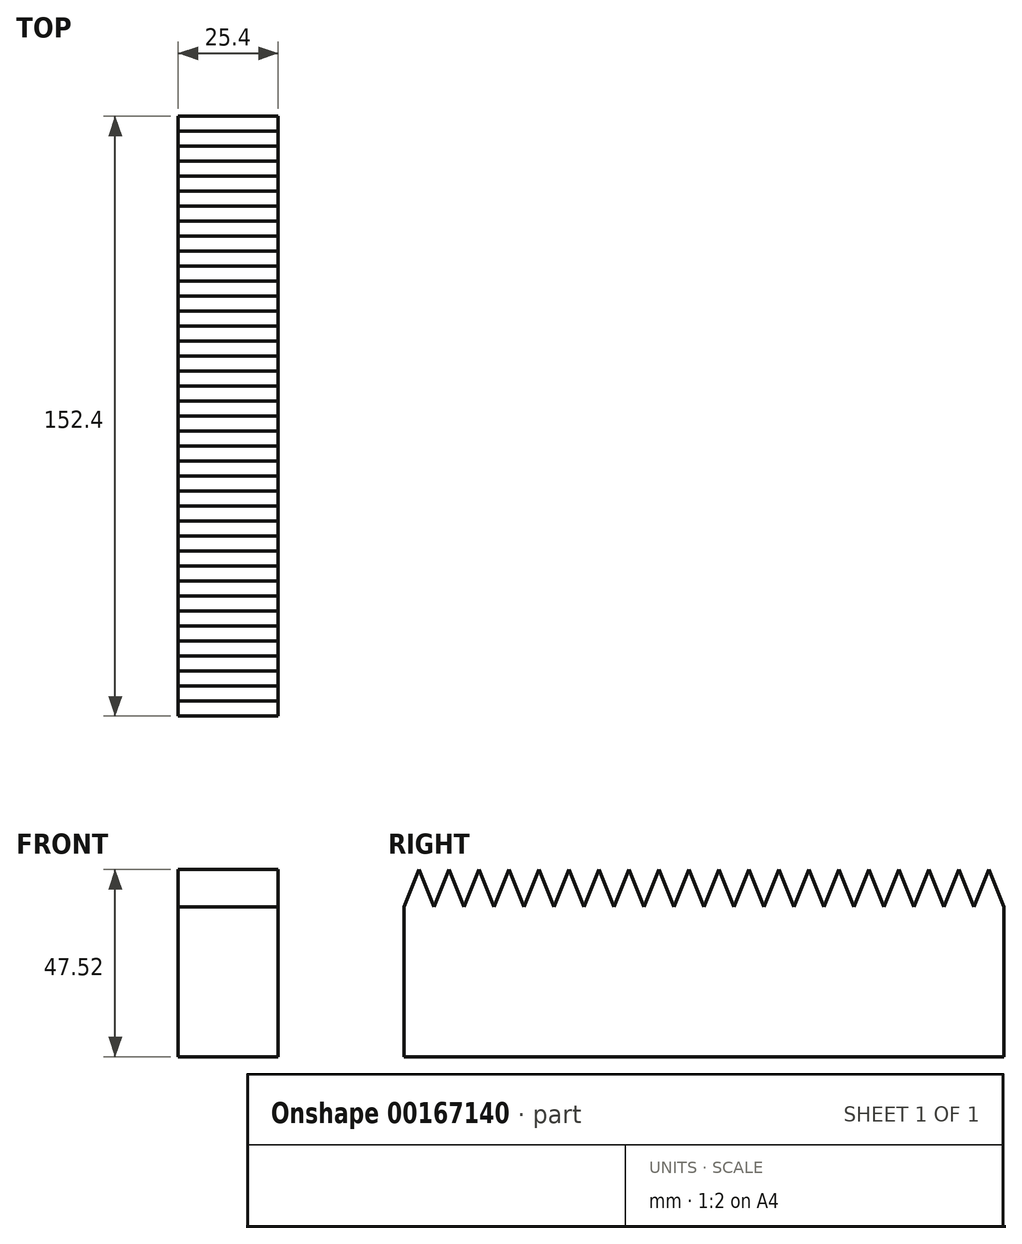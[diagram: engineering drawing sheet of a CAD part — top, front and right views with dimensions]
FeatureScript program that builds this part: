
annotation { "Feature Type Name" : "Feature", "Feature Type Description" : "" }
export const myFeature = defineFeature(function(context is Context, id is Id, definition is map)
    precondition{}
    {
        {
            var Q0;
            Q0=qCreatedBy(makeId("Right.planeOp"),FACE);
            var sketch = newSketch(context, id + "F0", { "sketchPlane" : qUnion([Q0])});
            skLineSegment(sketch, "E0.bottom", {"start": v(76.2, 19.05) * mm, "end": v(-76.2, 19.05) * mm});
            skLineSegment(sketch, "E0.top", {"start": v(76.2, -19.05) * mm, "end": v(-76.2, -19.05) * mm});
            skLineSegment(sketch, "E0.left", {"start": v(76.2, 19.05) * mm, "end": v(76.2, -19.05) * mm});
            skLineSegment(sketch, "E0.right", {"start": v(-76.2, 19.05) * mm, "end": v(-76.2, -19.05) * mm});
            skPoint(sketch, "E0.middle", {"position": v(0, 0) * mm});
            skLineSegment(sketch, "E1", {"start": v(-76.2, 19.05) * mm, "end": v(-72.39, 28.47) * mm});
            skLineSegment(sketch, "E2", {"start": v(-72.39, 28.47) * mm, "end": v(-68.58, 19.05) * mm});
            skLineSegment(sketch, "E3", {"start": v(-68.58, 19.05) * mm, "end": v(-76.2, 19.05) * mm});
            skLineSegment(sketch, "E4.1.0.0", {"start": v(-60.96, 19.05) * mm, "end": v(-68.58, 19.05) * mm});
            skLineSegment(sketch, "E4.1.0.1", {"start": v(-64.77, 28.47) * mm, "end": v(-60.96, 19.05) * mm});
            skLineSegment(sketch, "E4.1.0.2", {"start": v(-68.58, 19.05) * mm, "end": v(-64.77, 28.47) * mm});
            skLineSegment(sketch, "E4.2.0.0", {"start": v(-53.34, 19.05) * mm, "end": v(-60.96, 19.05) * mm});
            skLineSegment(sketch, "E4.2.0.1", {"start": v(-57.15, 28.47) * mm, "end": v(-53.34, 19.05) * mm});
            skLineSegment(sketch, "E4.2.0.2", {"start": v(-60.96, 19.05) * mm, "end": v(-57.15, 28.47) * mm});
            skLineSegment(sketch, "E4.3.0.0", {"start": v(-45.72, 19.05) * mm, "end": v(-53.34, 19.05) * mm});
            skLineSegment(sketch, "E4.3.0.1", {"start": v(-49.53, 28.47) * mm, "end": v(-45.72, 19.05) * mm});
            skLineSegment(sketch, "E4.3.0.2", {"start": v(-53.34, 19.05) * mm, "end": v(-49.53, 28.47) * mm});
            skLineSegment(sketch, "E4.4.0.0", {"start": v(-38.1, 19.05) * mm, "end": v(-45.72, 19.05) * mm});
            skLineSegment(sketch, "E4.4.0.1", {"start": v(-41.9, 28.47) * mm, "end": v(-38.1, 19.05) * mm});
            skLineSegment(sketch, "E4.4.0.2", {"start": v(-45.72, 19.05) * mm, "end": v(-41.9, 28.47) * mm});
            skLineSegment(sketch, "E4.5.0.0", {"start": v(-30.48, 19.05) * mm, "end": v(-38.1, 19.05) * mm});
            skLineSegment(sketch, "E4.5.0.1", {"start": v(-34.29, 28.47) * mm, "end": v(-30.48, 19.05) * mm});
            skLineSegment(sketch, "E4.5.0.2", {"start": v(-38.1, 19.05) * mm, "end": v(-34.29, 28.47) * mm});
            skLineSegment(sketch, "E4.6.0.0", {"start": v(-22.86, 19.05) * mm, "end": v(-30.48, 19.05) * mm});
            skLineSegment(sketch, "E4.6.0.1", {"start": v(-26.67, 28.47) * mm, "end": v(-22.86, 19.05) * mm});
            skLineSegment(sketch, "E4.6.0.2", {"start": v(-30.48, 19.05) * mm, "end": v(-26.67, 28.47) * mm});
            skLineSegment(sketch, "E4.7.0.0", {"start": v(-15.24, 19.05) * mm, "end": v(-22.86, 19.05) * mm});
            skLineSegment(sketch, "E4.7.0.1", {"start": v(-19.05, 28.47) * mm, "end": v(-15.24, 19.05) * mm});
            skLineSegment(sketch, "E4.7.0.2", {"start": v(-22.86, 19.05) * mm, "end": v(-19.05, 28.47) * mm});
            skLineSegment(sketch, "E4.8.0.0", {"start": v(-7.62, 19.05) * mm, "end": v(-15.24, 19.05) * mm});
            skLineSegment(sketch, "E4.8.0.1", {"start": v(-11.43, 28.47) * mm, "end": v(-7.62, 19.05) * mm});
            skLineSegment(sketch, "E4.8.0.2", {"start": v(-15.24, 19.05) * mm, "end": v(-11.43, 28.47) * mm});
            skLineSegment(sketch, "E4.9.0.0", {"start": v(0, 19.05) * mm, "end": v(-7.62, 19.05) * mm});
            skLineSegment(sketch, "E4.9.0.1", {"start": v(-3.8, 28.47) * mm, "end": v(0, 19.05) * mm});
            skLineSegment(sketch, "E4.9.0.2", {"start": v(-7.62, 19.05) * mm, "end": v(-3.8, 28.47) * mm});
            skLineSegment(sketch, "E4.10.0.0", {"start": v(7.62, 19.05) * mm, "end": v(0, 19.05) * mm});
            skLineSegment(sketch, "E4.10.0.1", {"start": v(3.81, 28.47) * mm, "end": v(7.62, 19.05) * mm});
            skLineSegment(sketch, "E4.10.0.2", {"start": v(0, 19.05) * mm, "end": v(3.81, 28.47) * mm});
            skLineSegment(sketch, "E4.11.0.0", {"start": v(15.24, 19.05) * mm, "end": v(7.62, 19.05) * mm});
            skLineSegment(sketch, "E4.11.0.1", {"start": v(11.43, 28.47) * mm, "end": v(15.24, 19.05) * mm});
            skLineSegment(sketch, "E4.11.0.2", {"start": v(7.62, 19.05) * mm, "end": v(11.43, 28.47) * mm});
            skLineSegment(sketch, "E4.12.0.0", {"start": v(22.86, 19.05) * mm, "end": v(15.24, 19.05) * mm});
            skLineSegment(sketch, "E4.12.0.1", {"start": v(19.05, 28.47) * mm, "end": v(22.86, 19.05) * mm});
            skLineSegment(sketch, "E4.12.0.2", {"start": v(15.24, 19.05) * mm, "end": v(19.05, 28.47) * mm});
            skLineSegment(sketch, "E4.13.0.0", {"start": v(30.48, 19.05) * mm, "end": v(22.86, 19.05) * mm});
            skLineSegment(sketch, "E4.13.0.1", {"start": v(26.67, 28.47) * mm, "end": v(30.48, 19.05) * mm});
            skLineSegment(sketch, "E4.13.0.2", {"start": v(22.86, 19.05) * mm, "end": v(26.67, 28.47) * mm});
            skLineSegment(sketch, "E4.14.0.0", {"start": v(38.1, 19.05) * mm, "end": v(30.48, 19.05) * mm});
            skLineSegment(sketch, "E4.14.0.1", {"start": v(34.3, 28.47) * mm, "end": v(38.1, 19.05) * mm});
            skLineSegment(sketch, "E4.14.0.2", {"start": v(30.48, 19.05) * mm, "end": v(34.3, 28.47) * mm});
            skLineSegment(sketch, "E4.15.0.0", {"start": v(45.72, 19.05) * mm, "end": v(38.1, 19.05) * mm});
            skLineSegment(sketch, "E4.15.0.1", {"start": v(41.91, 28.47) * mm, "end": v(45.72, 19.05) * mm});
            skLineSegment(sketch, "E4.15.0.2", {"start": v(38.1, 19.05) * mm, "end": v(41.91, 28.47) * mm});
            skLineSegment(sketch, "E4.16.0.0", {"start": v(53.34, 19.05) * mm, "end": v(45.72, 19.05) * mm});
            skLineSegment(sketch, "E4.16.0.1", {"start": v(49.53, 28.47) * mm, "end": v(53.34, 19.05) * mm});
            skLineSegment(sketch, "E4.16.0.2", {"start": v(45.72, 19.05) * mm, "end": v(49.53, 28.47) * mm});
            skLineSegment(sketch, "E4.17.0.0", {"start": v(60.96, 19.05) * mm, "end": v(53.34, 19.05) * mm});
            skLineSegment(sketch, "E4.17.0.1", {"start": v(57.15, 28.47) * mm, "end": v(60.96, 19.05) * mm});
            skLineSegment(sketch, "E4.17.0.2", {"start": v(53.34, 19.05) * mm, "end": v(57.15, 28.47) * mm});
            skLineSegment(sketch, "E4.18.0.0", {"start": v(68.58, 19.05) * mm, "end": v(60.96, 19.05) * mm});
            skLineSegment(sketch, "E4.18.0.1", {"start": v(64.77, 28.47) * mm, "end": v(68.58, 19.05) * mm});
            skLineSegment(sketch, "E4.18.0.2", {"start": v(60.96, 19.05) * mm, "end": v(64.77, 28.47) * mm});
            skLineSegment(sketch, "E4.19.0.0", {"start": v(76.2, 19.05) * mm, "end": v(68.58, 19.05) * mm});
            skLineSegment(sketch, "E4.19.0.1", {"start": v(72.4, 28.47) * mm, "end": v(76.2, 19.05) * mm});
            skLineSegment(sketch, "E4.19.0.2", {"start": v(68.58, 19.05) * mm, "end": v(72.4, 28.47) * mm});
            skLineSegment(sketch, "E4.direction1", {"start": v(-76.2, 19.05) * mm, "end": v(-68.58, 19.05) * mm, "construction": true});
            skSolve(sketch);
        }
        {
            var Q0;
            Q0 = qSketchRegion(id + "F0", true);
            extrude(context, id + "F1", {"entities" : qUnion([Q0]), "endBound" : BoundingType.SYMMETRIC, "depth" : 25.4 * mm});
        }
    });
